# Revit family: ok-Incepa_Bali_Cuba de Apoio_22016
name_source: partatom
category: Plumbing Fixtures
revit_build: Autodesk Revit MEP 2014 (Build: 20131024_2115(x64)
units: mm (PartAtom-declared; Revit-internal decimal feet)

## types (2) — shared parameters
Assembly Code = D2010400
Desenvolvido por = ofcdesk
Diâmetro Ponto de Esgoto = 40 mm
Incepa: Categoria = Cubas e Lavatórios
Incepa: Código = 22073
Incepa: Desenho Técnico = http://www.banheirosincepa.com.br
Incepa: Fabricante = Incepa
Incepa: Linha = Bali
Incepa: Link do Produto = http://www.banheirosincepa.com.br
Incepa: Norma = ABNT NBR 15097-1: 2011 - Requisitos e métodos de ensaio
Incepa: Produto = Louças
Incepa: Tipo = Cubas
Incepa: Versão = Autodesk Revit MEP 2014
Manufacturer = Incepa
Model = 22073
Raio Ponto de Esgoto = 20 mm
Selo de Qualidade ofcdesk = Standard
URL = http://www.banheirosincepa.com.br
WFU = 2
zero-valued in all types: CWFU, Default Elevation, HWFU

## per-type parameters (varying)
| type | Description | Incepa: Cores Disponíveis | Incepa: Descrição |
| 01 - Branco | Cuba de apoio cor branca (22073), 420 x 430 mm, linha Bali - Louças Incepa | Branco | Cuba de apoio cor branca (22073), 420 x 430 mm, linha Bali - Louças Incepa |
| 57 - Biscuit | Cuba de apoio cor biscuit (22073), 420 x 430 mm, linha Bali - Louças Incepa | Biscuit | Cuba de apoio cor biscuit (22073), 420 x 430 mm, linha Bali - Louças Incepa |

## geometry (parser evidence)
native form markers: Blend x4, Sweep x10
no freeform markers — native parametric forms only
